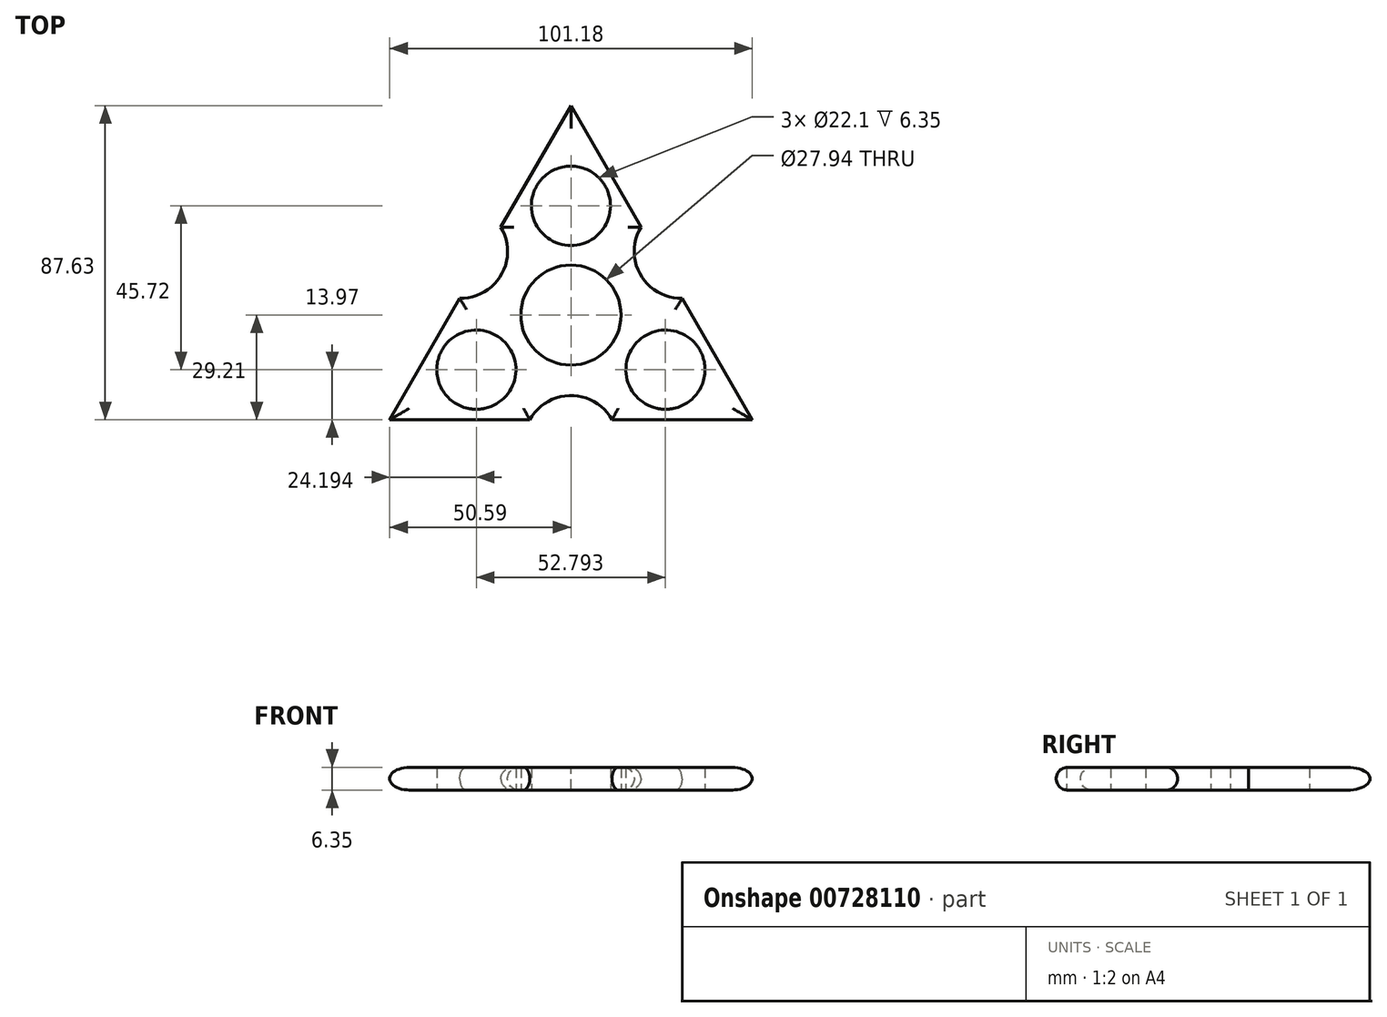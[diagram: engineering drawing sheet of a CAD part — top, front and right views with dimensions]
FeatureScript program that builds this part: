
annotation { "Feature Type Name" : "Feature", "Feature Type Description" : "" }
export const myFeature = defineFeature(function(context is Context, id is Id, definition is map)
    precondition{}
    {
        {
            var Q0;
            Q0=qCreatedBy(makeId("Top.planeOp"),FACE);
            var sketch = newSketch(context, id + "F0", { "sketchPlane" : qUnion([Q0])});
            skCircle(sketch, "E0", {"center": v(0, 0) * mm, "radius": 11.05 * mm});
            skCircle(sketch, "E1", {"center": v(0, 0) * mm, "radius": 13.97 * mm});
            skLineSegment(sketch, "E2", {"start": v(0, 0) * mm, "end": v(0, 30.48) * mm});
            skCircle(sketch, "E3", {"center": v(0, 30.48) * mm, "radius": 11.05 * mm});
            skCircle(sketch, "E4", {"center": v(0, 30.48) * mm, "radius": 13.97 * mm});
            skCircle(sketch, "E5.1.0", {"center": v(-26.4, -15.24) * mm, "radius": 11.05 * mm});
            skCircle(sketch, "E5.1.1", {"center": v(-26.4, -15.24) * mm, "radius": 13.97 * mm});
            skCircle(sketch, "E5.2.0", {"center": v(26.4, -15.24) * mm, "radius": 11.05 * mm});
            skCircle(sketch, "E5.2.1", {"center": v(26.4, -15.24) * mm, "radius": 13.97 * mm});
            skLineSegment(sketch, "E6", {"start": v(0, 30.48) * mm, "end": v(0, 58.42) * mm});
            skLineSegment(sketch, "E7", {"start": v(0, 58.42) * mm, "end": v(-19.57, 24.53) * mm});
            skLineSegment(sketch, "E8", {"start": v(-50.6, -29.2) * mm, "end": v(-11.46, -29.21) * mm});
            skLineSegment(sketch, "E9", {"start": v(0, 58.42) * mm, "end": v(19.57, 24.53) * mm});
            skLineSegment(sketch, "E10", {"start": v(-9.57, 5.52) * mm, "end": v(-12.1, 6.99) * mm});
            skArc(sketch, "E11", {"start": v(-31.03, 4.68) * mm, "mid": v(-19.43, 11.22) * mm, "end": v(-19.57, 24.53) * mm});
            skLineSegment(sketch, "E12.trimOffspring", {"start": v(-31.03, 4.68) * mm, "end": v(-50.6, -29.2) * mm});
            skArc(sketch, "E13.1.0", {"start": v(11.46, -29.21) * mm, "mid": v(0, -22.44) * mm, "end": v(-11.46, -29.21) * mm});
            skArc(sketch, "E13.2.0", {"start": v(19.57, 24.53) * mm, "mid": v(19.43, 11.22) * mm, "end": v(31.03, 4.68) * mm});
            skLineSegment(sketch, "E14.trimOffspring", {"start": v(31.03, 4.68) * mm, "end": v(50.6, -29.21) * mm});
            skLineSegment(sketch, "E15.trimOffspring", {"start": v(11.46, -29.21) * mm, "end": v(50.6, -29.21) * mm});
            skSolve(sketch);
        }
        {
            var Q0;
            Q0 = qSketchRegion(id + "F0", true);
            extrude(context, id + "F1", {"entities" : qUnion([Q0]), "depth" : 6.35 * mm, "offsetDistance" : 25.4 * mm});
        }
        {
            var Q0;
            Q0=makeQuery(id+"F1.opExtrude","CAP_EDGE",EDGE,{"disambiguationData":[OSD([sQuery(id+"F0.wireOp",EDGE,"E7")])],"isStart":false});
            var Q1;
            Q1=makeQuery(id+"F1.opExtrude","CAP_EDGE",EDGE,{"disambiguationData":[OSD([sQuery(id+"F0.wireOp",EDGE,"E9")])],"isStart":false});
            var Q2;
            Q2=makeQuery(id+"F1.opExtrude","CAP_EDGE",EDGE,{"disambiguationData":[OSD([sQuery(id+"F0.wireOp",EDGE,"E13.2.0")])],"isStart":false});
            var Q3;
            Q3=makeQuery(id+"F1.opExtrude","CAP_EDGE",EDGE,{"disambiguationData":[OSD([sQuery(id+"F0.wireOp",EDGE,"E11")])],"isStart":false});
            var Q4;
            Q4=makeQuery(id+"F1.opExtrude","CAP_EDGE",EDGE,{"disambiguationData":[OSD([sQuery(id+"F0.wireOp",EDGE,"E12.trimOffspring")])],"isStart":false});
            var Q5;
            Q5=makeQuery(id+"F1.opExtrude","CAP_EDGE",EDGE,{"disambiguationData":[OSD([sQuery(id+"F0.wireOp",EDGE,"E8")])],"isStart":false});
            var Q6;
            Q6=makeQuery(id+"F1.opExtrude","CAP_EDGE",EDGE,{"disambiguationData":[OSD([sQuery(id+"F0.wireOp",EDGE,"E13.1.0")])],"isStart":false});
            var Q7;
            Q7=makeQuery(id+"F1.opExtrude","CAP_EDGE",EDGE,{"disambiguationData":[OSD([sQuery(id+"F0.wireOp",EDGE,"E15.trimOffspring")])],"isStart":false});
            var Q8;
            Q8=makeQuery(id+"F1.opExtrude","CAP_EDGE",EDGE,{"disambiguationData":[OSD([sQuery(id+"F0.wireOp",EDGE,"E14.trimOffspring")])],"isStart":false});
            var Q9;
            Q9=makeQuery(id+"F1.opExtrude","CAP_EDGE",EDGE,{"disambiguationData":[OSD([sQuery(id+"F0.wireOp",EDGE,"E9")])],"isStart":true});
            var Q10;
            Q10=makeQuery(id+"F1.opExtrude","CAP_EDGE",EDGE,{"disambiguationData":[OSD([sQuery(id+"F0.wireOp",EDGE,"E13.2.0")])],"isStart":true});
            var Q11;
            Q11=makeQuery(id+"F1.opExtrude","CAP_EDGE",EDGE,{"disambiguationData":[OSD([sQuery(id+"F0.wireOp",EDGE,"E14.trimOffspring")])],"isStart":true});
            var Q12;
            Q12=makeQuery(id+"F1.opExtrude","CAP_EDGE",EDGE,{"disambiguationData":[OSD([sQuery(id+"F0.wireOp",EDGE,"E15.trimOffspring")])],"isStart":true});
            var Q13;
            Q13=makeQuery(id+"F1.opExtrude","CAP_EDGE",EDGE,{"disambiguationData":[OSD([sQuery(id+"F0.wireOp",EDGE,"E13.1.0")])],"isStart":true});
            var Q14;
            Q14=makeQuery(id+"F1.opExtrude","CAP_EDGE",EDGE,{"disambiguationData":[OSD([sQuery(id+"F0.wireOp",EDGE,"E8")])],"isStart":true});
            var Q15;
            Q15=makeQuery(id+"F1.opExtrude","CAP_EDGE",EDGE,{"disambiguationData":[OSD([sQuery(id+"F0.wireOp",EDGE,"E12.trimOffspring")])],"isStart":true});
            var Q16;
            Q16=makeQuery(id+"F1.opExtrude","CAP_EDGE",EDGE,{"disambiguationData":[OSD([sQuery(id+"F0.wireOp",EDGE,"E11")])],"isStart":true});
            var Q17;
            Q17=makeQuery(id+"F1.opExtrude","CAP_EDGE",EDGE,{"disambiguationData":[OSD([sQuery(id+"F0.wireOp",EDGE,"E7")])],"isStart":true});
            fillet(context, id + "F2", {"entities" : qUnion([Q0, Q1, Q2, Q3, Q4, Q5, Q6, Q7, Q8, Q9, Q10, Q11, Q12, Q13, Q14, Q15, Q16, Q17]), "radius" : 3.17 * mm, "tangentPropagation" : true, "allowEdgeOverflow" : false});
        }
    });
